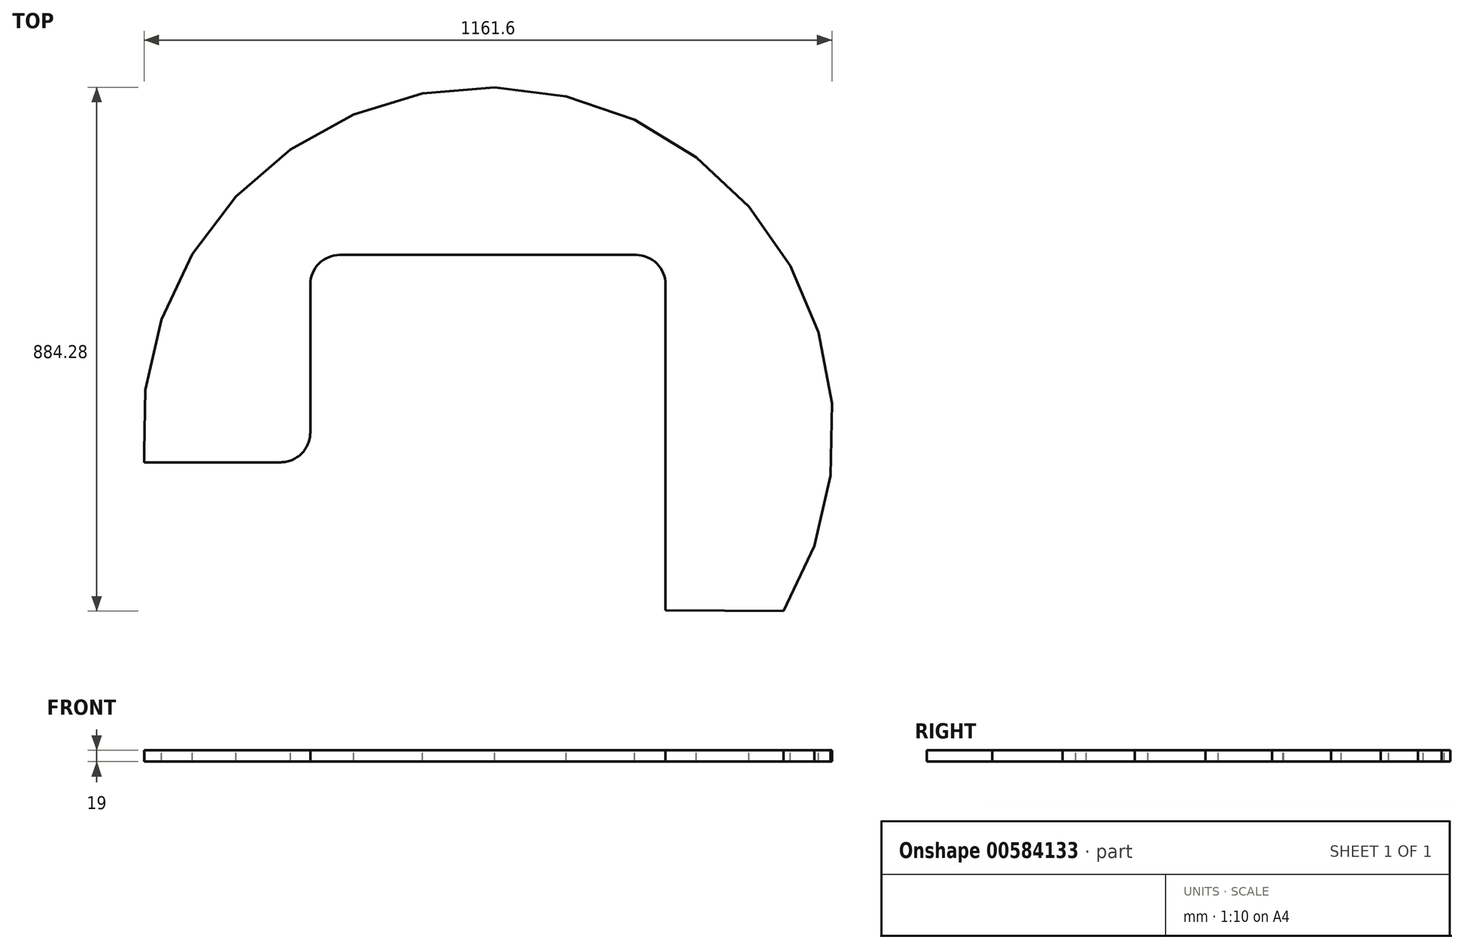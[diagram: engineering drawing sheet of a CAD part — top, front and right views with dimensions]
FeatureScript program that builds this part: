
annotation { "Feature Type Name" : "Feature", "Feature Type Description" : "" }
export const myFeature = defineFeature(function(context is Context, id is Id, definition is map)
    precondition{}
    {
        {
            var Q0;
            Q0=qCreatedBy(makeId("Top.planeOp"),FACE);
            var sketch = newSketch(context, id + "F0", { "sketchPlane" : qUnion([Q0])});
            skLineSegment(sketch, "E0", {"start": v(0, 0) * mm, "end": v(-0.78, 0) * mm});
            skLineSegment(sketch, "E1", {"start": v(-200, 16.7) * mm, "end": v(-200, 550) * mm});
            skLineSegment(sketch, "E2", {"start": v(-250, 600) * mm, "end": v(-750, 600) * mm});
            skLineSegment(sketch, "E3", {"start": v(-800, 550) * mm, "end": v(-800, 300.06) * mm});
            skPoint(sketch, "E4.visualSharp", {"position": v(-800, 600) * mm});
            skArc(sketch, "E4.filletArc", {"start": v(-750, 600) * mm, "mid": v(-785.36, 585.36) * mm, "end": v(-800, 550) * mm});
            skPoint(sketch, "E5.visualSharp", {"position": v(-200, 600) * mm});
            skArc(sketch, "E5.filletArc", {"start": v(-200, 550) * mm, "mid": v(-214.64, 585.36) * mm, "end": v(-250, 600) * mm});
            skPoint(sketch, "E6.visualSharp", {"position": v(-800, 250) * mm});
            skArc(sketch, "E6.filletArc", {"start": v(-850.06, 250.06) * mm, "mid": v(-814.66, 264.68) * mm, "end": v(-800, 300.06) * mm});
            skLineSegment(sketch, "E7.0", {"start": v(-1080.63, 268.06) * mm, "end": v(-1078.6, 372.2) * mm});
            skLineSegment(sketch, "E7.1", {"start": v(-1078.6, 372.2) * mm, "end": v(-1050.96, 490.91) * mm});
            skLineSegment(sketch, "E7.2", {"start": v(-1050.96, 490.91) * mm, "end": v(-999.22, 601.3) * mm});
            skLineSegment(sketch, "E7.3", {"start": v(-999.22, 601.3) * mm, "end": v(-925.67, 698.5) * mm});
            skLineSegment(sketch, "E7.4", {"start": v(-925.67, 698.5) * mm, "end": v(-833.52, 778.3) * mm});
            skLineSegment(sketch, "E7.5", {"start": v(-833.52, 778.3) * mm, "end": v(-726.78, 837.19) * mm});
            skLineSegment(sketch, "E7.6", {"start": v(-726.78, 837.19) * mm, "end": v(-610.14, 872.6) * mm});
            skLineSegment(sketch, "E7.7", {"start": v(-610.14, 872.6) * mm, "end": v(-488.68, 882.99) * mm});
            skLineSegment(sketch, "E7.8", {"start": v(-488.68, 882.99) * mm, "end": v(-367.72, 867.9) * mm});
            skLineSegment(sketch, "E7.9", {"start": v(-367.72, 867.9) * mm, "end": v(-252.54, 827.98) * mm});
            skLineSegment(sketch, "E7.10", {"start": v(-252.54, 827.98) * mm, "end": v(-148.17, 765) * mm});
            skLineSegment(sketch, "E7.11", {"start": v(-148.17, 765) * mm, "end": v(-59.19, 681.68) * mm});
            skLineSegment(sketch, "E7.12", {"start": v(-59.19, 681.68) * mm, "end": v(10.54, 581.7) * mm});
            skLineSegment(sketch, "E7.13", {"start": v(10.54, 581.7) * mm, "end": v(57.95, 469.4) * mm});
            skLineSegment(sketch, "E7.14", {"start": v(57.95, 469.4) * mm, "end": v(80.97, 349.68) * mm});
            skLineSegment(sketch, "E7.15", {"start": v(80.97, 349.68) * mm, "end": v(78.6, 227.8) * mm});
            skLineSegment(sketch, "E7.16", {"start": v(78.6, 227.8) * mm, "end": v(50.96, 109.09) * mm});
            skLineSegment(sketch, "E7.17", {"start": v(50.96, 109.09) * mm, "end": v(-0.78, -1.3) * mm});
            skArc(sketch, "E8.trimOffspring", {"start": v(-0.78, -1.3) * mm, "mid": v(-0.39, -0.65) * mm, "end": v(0, 0) * mm, "construction": true});
            skLineSegment(sketch, "E9", {"start": v(-0.78, -1.3) * mm, "end": v(-0.78, 0) * mm});
            skPoint(sketch, "E10.orphan", {"position": v(-200, 0) * mm});
            skLineSegment(sketch, "E11", {"start": v(-0.78, -1.3) * mm, "end": v(-200, 0) * mm});
            skLineSegment(sketch, "E12", {"start": v(-200, 16.7) * mm, "end": v(-200, 0) * mm});
            skLineSegment(sketch, "E13", {"start": v(-1080.63, 268.06) * mm, "end": v(-1080.63, 250.06) * mm});
            skLineSegment(sketch, "E14", {"start": v(-850.06, 250.06) * mm, "end": v(-1080.63, 250.06) * mm});
            skSolve(sketch);
        }
        {
            var Q0;
            Q0=qSketchRegion(id+"F0",true);
            extrude(context, id + "F1", {"entities" : qUnion([Q0]), "oppositeDirection" : true, "depth" : 19 * mm, "offsetDistance" : 25 * mm});
        }
    });
